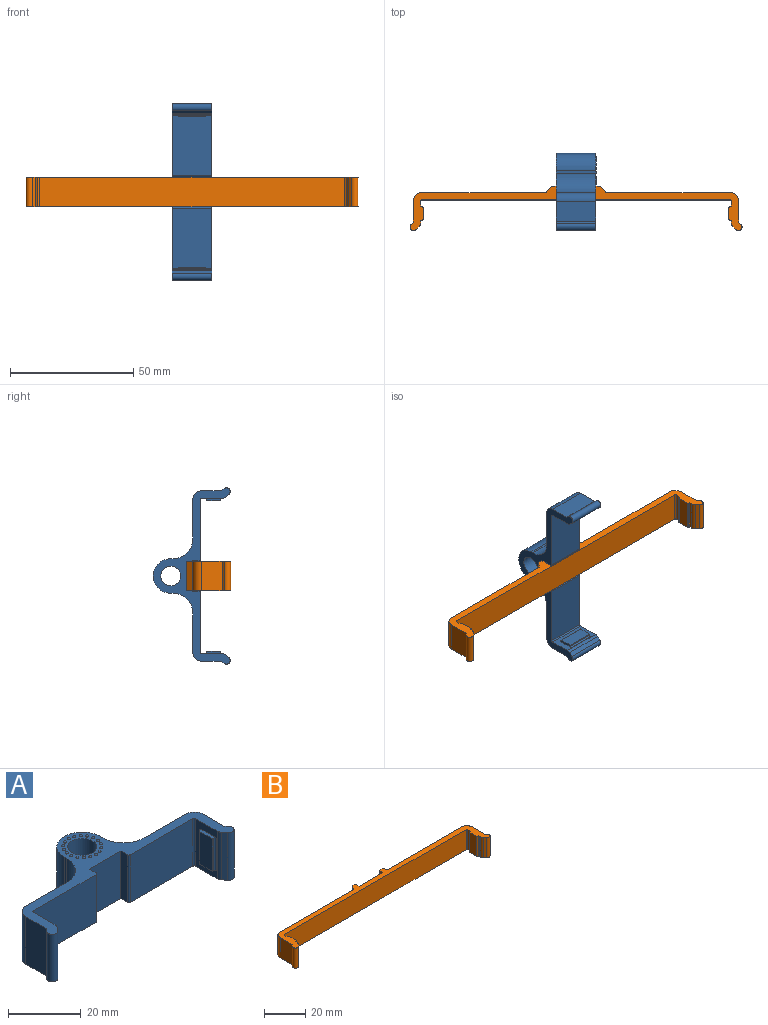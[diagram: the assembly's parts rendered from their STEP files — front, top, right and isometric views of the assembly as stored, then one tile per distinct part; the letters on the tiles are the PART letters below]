
ASSEMBLY  parts=2 mates=1
PART A: 65 faces, bbox 71.5x31.1x16.4 mm
  f0: cylinder r=4mm len=16mm, axis (0,0,-1), area 402.1mm2, adj f23,f45
  f1: plane 16x12.2mm, normal (0,-1,0), area 195.2mm2, adj f2,f23,f24,f45
  f2: plane 16x2.6mm, normal (-1,0,0), area 41.6mm2, adj f1,f3,f23,f45
  f3: cylinder r=0.5mm len=16mm, axis (0,0,-1), area 12.6mm2, adj f2,f4,f23,f45
  f4: plane 24.4x16mm, normal (0,-1,0), area 390.4mm2, adj f3,f5,f23,f45
  f5: cylinder r=0.5mm len=16mm, axis (0,0,-1), area 12.6mm2, adj f4,f11,f23,f45
  f6: plane 11x0.5mm, normal (0,1,0), area 5.5mm2, adj f7,f11,f22,f44
  f7: cylinder r=0.5mm len=11mm, axis (0,0,-1), area 8.6mm2, adj f6,f8,f22,f44
  f8: plane 11x5mm, normal (-1,0,0), area 55mm2, adj f7,f9,f22,f44
  f9: plane 11x0.5mm, normal (0,-1,0), area 5.5mm2, adj f8,f10,f22,f44
  f10: cylinder r=0.5mm len=11mm, axis (0,0,-1), area 8.6mm2, adj f9,f11,f22,f44
  f11: plane 16x8.4mm, normal (-1,0,0), area 68.4mm2, adj f5,f6,f10,f12,f22,f23,f44,f45
  f12: cylinder r=2mm len=16mm, axis (0,0,-1), area 21.6mm2, adj f11,f13,f23,f45
  f13: plane 16x1.4mm, normal (-0.78,-0.62,0), area 28.8mm2, adj f12,f14,f23,f45
  f14: cylinder r=1.5mm len=16mm, axis (0,0,-1), area 75.4mm2, adj f13,f15,f23,f45
  f15: plane 16x1.13mm, normal (0.78,0.62,0), area 23.2mm2, adj f14,f16,f23,f45
  f16: plane 16x8.05mm, normal (1,0,0), area 128.8mm2, adj f15,f17,f23,f45
  f17: cylinder r=3.5mm len=16mm, axis (0,0,-1), area 88mm2, adj f16,f18,f23,f45
  f18: plane 16x16mm, normal (0,1,0), area 256mm2, adj f17,f19,f23,f45
  f19: cylinder r=8mm len=16mm, axis (0,0,-1), area 201.1mm2, adj f18,f20,f23,f45
  f20: plane 16x1mm, normal (1,0,0), area 16mm2, adj f19,f21,f23,f45
  f21: cylinder r=7mm len=16mm, axis (0,0,-1), area 351.9mm2, adj f20,f23,f42,f45
  f22: plane 6x1mm, normal (0,0,1), area 5.5mm2, adj f6,f7,f8,f9,f10,f11
  f23: plane 71.47x31.12mm, normal (0,0,1), area 408.3mm2, adj f0,f1,f2,f3,f4,f5,f11,f12
  f24: plane 16x2.6mm, normal (1,0,0), area 41.6mm2, adj f1,f23,f25,f45
  f25: cylinder r=0.5mm len=16mm, axis (0,0,-1), area 12.6mm2, adj f23,f24,f26,f45
  f26: plane 24.4x16mm, normal (0,-1,0), area 390.4mm2, adj f23,f25,f27,f45
  f27: cylinder r=0.5mm len=16mm, axis (0,0,-1), area 12.6mm2, adj f23,f26,f33,f45
  f28: plane 11x0.5mm, normal (0,1,0), area 5.5mm2, adj f29,f33,f43,f46
  f29: cylinder r=0.5mm len=11mm, axis (0,0,-1), area 8.6mm2, adj f28,f30,f43,f46
  f30: plane 11x5mm, normal (1,0,0), area 55mm2, adj f29,f31,f43,f46
  f31: plane 11x0.5mm, normal (0,-1,0), area 5.5mm2, adj f30,f32,f43,f46
  f32: cylinder r=0.5mm len=11mm, axis (0,0,-1), area 8.6mm2, adj f31,f33,f43,f46
  f33: plane 16x8.4mm, normal (1,0,0), area 68.4mm2, adj f23,f27,f28,f32,f34,f43,f45,f46
  f34: cylinder r=2mm len=16mm, axis (0,0,-1), area 21.6mm2, adj f23,f33,f35,f45
  f35: plane 16x1.4mm, normal (0.78,-0.62,0), area 28.8mm2, adj f23,f34,f36,f45
  f36: cylinder r=1.5mm len=16mm, axis (0,0,-1), area 75.4mm2, adj f23,f35,f37,f45
  f37: plane 16x1.13mm, normal (-0.78,0.62,0), area 23.2mm2, adj f23,f36,f38,f45
  f38: plane 16x8.05mm, normal (-1,0,0), area 128.8mm2, adj f23,f37,f39,f45
  f39: cylinder r=3.5mm len=16mm, axis (0,0,-1), area 88mm2, adj f23,f38,f40,f45
  f40: plane 16x16mm, normal (0,1,0), area 256mm2, adj f23,f39,f41,f45
  f41: cylinder r=8mm len=16mm, axis (0,0,-1), area 201.1mm2, adj f23,f40,f42,f45
  f42: plane 16x1mm, normal (-1,0,0), area 16mm2, adj f21,f23,f41,f45
  f43: plane 6x1mm, normal (0,0,1), area 5.5mm2, adj f28,f29,f30,f31,f32,f33
  f44: plane 6x1mm, normal (0,0,-1), area 5.5mm2, adj f6,f7,f8,f9,f10,f11
  f45: plane 71.47x31.12mm, normal (0,0,-1), area 417.3mm2, adj f0,f1,f2,f3,f4,f5,f11,f12
  f46: plane 6x1mm, normal (0,0,-1), area 5.5mm2, adj f28,f29,f30,f31,f32,f33
  f47: sphere r=0.4mm, area 1mm2, adj f23
  f48: sphere r=0.4mm, area 1mm2, adj f23
  f49: sphere r=0.4mm, area 1mm2, adj f23
  f50: sphere r=0.4mm, area 1mm2, adj f23
  f51: sphere r=0.4mm, area 1mm2, adj f23
  f52: sphere r=0.4mm, area 1mm2, adj f23
  f53: sphere r=0.4mm, area 1mm2, adj f23
  f54: sphere r=0.4mm, area 1mm2, adj f23
  f55: sphere r=0.4mm, area 1mm2, adj f23
  f56: sphere r=0.4mm, area 1mm2, adj f23
  f57: sphere r=0.4mm, area 1mm2, adj f23
  f58: sphere r=0.4mm, area 1mm2, adj f23
  f59: sphere r=0.4mm, area 1mm2, adj f23
  f60: sphere r=0.4mm, area 1mm2, adj f23
  f61: sphere r=0.4mm, area 1mm2, adj f23
  f62: sphere r=0.4mm, area 1mm2, adj f23
  f63: sphere r=0.4mm, area 1mm2, adj f23
  f64: sphere r=0.4mm, area 1mm2, adj f23
PART B: 44 faces, bbox 134.7x17.9x12 mm
  f0: cylinder r=0.1mm len=12mm, axis (0,0,-1), area 1.9mm2, adj f1,f21,f22,f23
  f1: plane 12x1.07mm, normal (-1,0,0), area 12.9mm2, adj f0,f2,f22,f23
  f2: cylinder r=2mm len=12mm, axis (0,0,-1), area 18.8mm2, adj f1,f3,f22,f23
  f3: plane 12x1.18mm, normal (-0.71,-0.71,0), area 20.1mm2, adj f2,f4,f22,f23
  f4: cylinder r=1.5mm len=12mm, axis (0,0,-1), area 56.5mm2, adj f3,f5,f22,f23
  f5: plane 12x0.89mm, normal (0.71,0.71,0), area 15.1mm2, adj f4,f6,f22,f23
  f6: plane 12x8.46mm, normal (1,0,0), area 101.5mm2, adj f5,f7,f22,f23
  f7: cylinder r=3.5mm len=12mm, axis (0,0,-1), area 66mm2, adj f6,f8,f22,f23
  f8: plane 50.4x12mm, normal (0,1,0), area 604.8mm2, adj f7,f9,f22,f23
  f9: plane 12x2.5mm, normal (0.78,0.62,0), area 38.4mm2, adj f8,f10,f22,f23
  f10: plane 12x2mm, normal (0,1,0), area 24mm2, adj f9,f11,f22,f23
  f11: plane 12x2.5mm, normal (-1,0,0), area 30mm2, adj f10,f12,f22,f23
  f12: plane 16.2x12mm, normal (0,1,0), area 194.4mm2, adj f11,f22,f23,f35
  f13: plane 125x12mm, normal (0,-1,0), area 1500mm2, adj f14,f22,f23,f36
  f14: cylinder r=0.5mm len=12mm, axis (0,0,-1), area 9.4mm2, adj f13,f15,f22,f23
  f15: plane 12x2mm, normal (-1,0,0), area 24mm2, adj f14,f16,f22,f23
  f16: cylinder r=0.1mm len=12mm, axis (0,0,-1), area 1.9mm2, adj f15,f17,f22,f23
  f17: plane 12x0.4mm, normal (0,1,0), area 4.8mm2, adj f16,f18,f22,f23
  f18: cylinder r=0.5mm len=12mm, axis (0,0,-1), area 9.4mm2, adj f17,f19,f22,f23
  f19: plane 12x4.6mm, normal (-1,0,0), area 55.2mm2, adj f18,f20,f22,f23
  f20: cylinder r=0.5mm len=12mm, axis (0,0,-1), area 9.4mm2, adj f19,f21,f22,f23
  f21: plane 12x0.4mm, normal (0,-1,0), area 4.8mm2, adj f0,f20,f22,f23
  f22: plane 134.66x17.91mm, normal (0,0,1), area 492.5mm2, adj f0,f1,f2,f3,f4,f5,f6,f7
  f23: plane 134.66x17.91mm, normal (0,0,-1), area 492.5mm2, adj f0,f1,f2,f3,f4,f5,f6,f7
  f24: cylinder r=0.1mm len=12mm, axis (0,0,-1), area 1.9mm2, adj f22,f23,f25,f43
  f25: plane 12x1.07mm, normal (1,0,0), area 12.9mm2, adj f22,f23,f24,f26
  f26: cylinder r=2mm len=12mm, axis (0,0,-1), area 18.8mm2, adj f22,f23,f25,f27
  f27: plane 12x1.18mm, normal (0.71,-0.71,0), area 20.1mm2, adj f22,f23,f26,f28
  f28: cylinder r=1.5mm len=12mm, axis (0,0,-1), area 56.5mm2, adj f22,f23,f27,f29
  f29: plane 12x0.89mm, normal (-0.71,0.71,0), area 15.1mm2, adj f22,f23,f28,f30
  f30: plane 12x8.46mm, normal (-1,0,0), area 101.5mm2, adj f22,f23,f29,f31
  f31: cylinder r=3.5mm len=12mm, axis (0,0,-1), area 66mm2, adj f22,f23,f30,f32
  f32: plane 50.4x12mm, normal (0,1,0), area 604.8mm2, adj f22,f23,f31,f33
  f33: plane 12x2.5mm, normal (-0.78,0.62,0), area 38.4mm2, adj f22,f23,f32,f34
  f34: plane 12x2mm, normal (0,1,0), area 24mm2, adj f22,f23,f33,f35
  f35: plane 12x2.5mm, normal (1,0,0), area 30mm2, adj f12,f22,f23,f34
  f36: cylinder r=0.5mm len=12mm, axis (0,0,-1), area 9.4mm2, adj f13,f22,f23,f37
  f37: plane 12x2mm, normal (1,0,0), area 24mm2, adj f22,f23,f36,f38
  f38: cylinder r=0.1mm len=12mm, axis (0,0,-1), area 1.9mm2, adj f22,f23,f37,f39
  f39: plane 12x0.4mm, normal (0,1,0), area 4.8mm2, adj f22,f23,f38,f40
  f40: cylinder r=0.5mm len=12mm, axis (0,0,-1), area 9.4mm2, adj f22,f23,f39,f41
  f41: plane 12x4.6mm, normal (1,0,0), area 55.2mm2, adj f22,f23,f40,f42
  f42: cylinder r=0.5mm len=12mm, axis (0,0,-1), area 9.4mm2, adj f22,f23,f41,f43
  f43: plane 12x0.4mm, normal (0,-1,0), area 4.8mm2, adj f22,f23,f24,f42
PLACE A rot(axis=(0,1,0),90deg) t=(0,-33.1,6)mm
PLACE B at identity
MATE fastened A.f1 <-> B.f12  axis (0,-1,0) through (0,-30,6)mm
